# Revit family: HEFTY_4000K_12000LM_92W
name_source: partatom
category: Lighting Fixtures
units: mm (PartAtom-declared; Revit-internal decimal feet)

## family parameters
Always vertical = Yes
Cut with Voids When Loaded = No
Host = Ceiling
Light Source = Yes
OmniClass Number = 23.80.70.11
OmniClass Title = Luminaries for Internal Lighting
Part Type = Normal
Room Calculation Point = No
Round Connector Dimension = Use Diameter
Shared = No

## types (1)
- Type 1
    Angle d'éclairage = 90°
    Color Filter = 16777215
    Default Elevation = 0 mm  [stored 0 ft]
    Diffuseur = Polycarbonate Opale
    Dimensions = 1220x190x90 mm
    Dimming Lamp Color Temperature Shift = <None>
    Driver = Driver Osram
    Durée de vie = 50 000 heures
    Emit Shape Visible in Rendering = No
    Emit from Rectangle Length = 1219 mm
    Emit from Rectangle Width = 610 mm  [stored 2.00131 ft]
    IRC = >80
    Maintien du flux = L80B10 (50 000 heures)
    Matériau = Acier galvanisé blanc
    Photometric Web File = google_eulumdat_converter (6).ies
    Poids = 6 kg
    Puissance nominale = 92W
    SDCM = <3
    Tension = AC 220-240V
    Tilt Angle = 90.00°
    Type = Luminaire industriel
    Type de lampe = LED Mid Power

note: [stored X ft] marks values corroborated as IEEE doubles in the binary element streams (Revit-internal decimal feet)

## geometry (parser evidence)
native form markers: Sweep x1
no freeform markers — native parametric forms only
